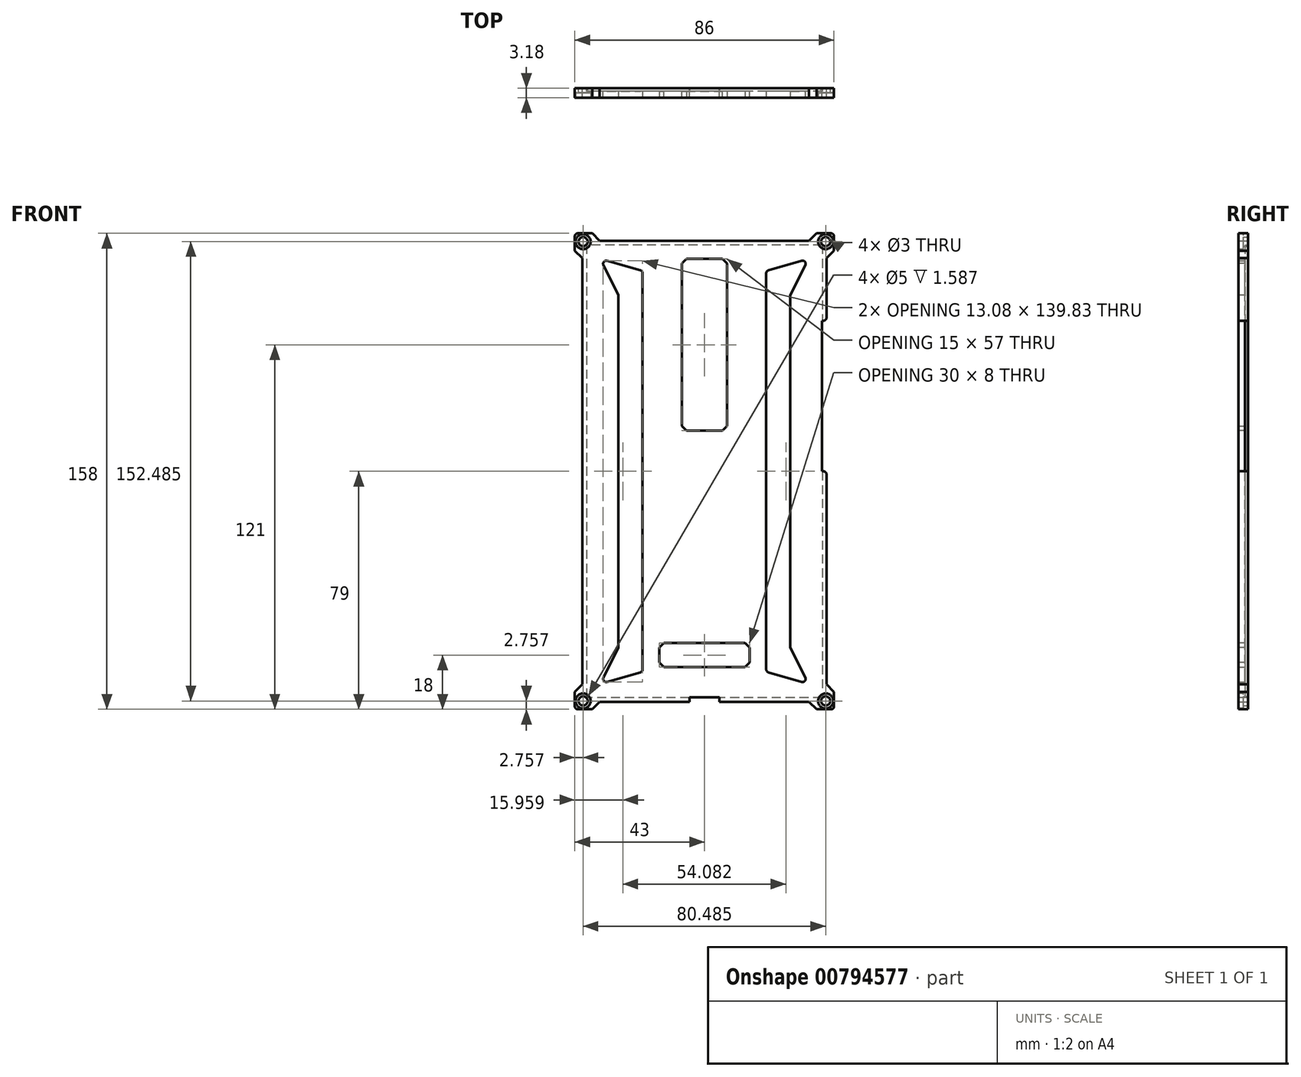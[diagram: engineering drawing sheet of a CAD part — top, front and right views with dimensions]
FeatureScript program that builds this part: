
annotation { "Feature Type Name" : "Feature", "Feature Type Description" : "" }
export const myFeature = defineFeature(function(context is Context, id is Id, definition is map)
    precondition{}
    {
        {
            var Q0;
            Q0=qCreatedBy(makeId("Front.planeOp"),FACE);
            var sketch = newSketch(context, id + "F0", { "sketchPlane" : qUnion([Q0])});
            skLineSegment(sketch, "E0.bottom", {"start": v(39, 75) * mm, "end": v(-39, 75) * mm});
            skLineSegment(sketch, "E0.top", {"start": v(39, -75) * mm, "end": v(-39, -75) * mm});
            skLineSegment(sketch, "E0.left", {"start": v(39, 75) * mm, "end": v(39, -75) * mm});
            skLineSegment(sketch, "E0.right", {"start": v(-39, 75) * mm, "end": v(-39, -75) * mm});
            skPoint(sketch, "E0.middle", {"position": v(0, 0) * mm});
            skSolve(sketch);
        }
        {
            var Q0;
            Q0=qCreatedBy(makeId("Front.planeOp"),FACE);
            var sketch = newSketch(context, id + "F1", { "sketchPlane" : qUnion([Q0])});
            skPoint(sketch, "E1.middle", {"position": v(0, 0) * mm});
            skLineSegment(sketch, "E2.bottom", {"start": v(43, 79) * mm, "end": v(37.24, 79) * mm});
            skLineSegment(sketch, "E2.top", {"start": v(43, -79) * mm, "end": v(37.24, -79) * mm});
            skLineSegment(sketch, "E2.left", {"start": v(43, 79) * mm, "end": v(43, 73.24) * mm});
            skLineSegment(sketch, "E2.right", {"start": v(-43, 79) * mm, "end": v(-43, 73.24) * mm});
            skLineSegment(sketch, "E3.bottom", {"start": v(40.5, 50) * mm, "end": v(39, 50) * mm});
            skLineSegment(sketch, "E3.top", {"start": v(40.5, 0) * mm, "end": v(39, 0) * mm});
            skLineSegment(sketch, "E3.right", {"start": v(39, 50) * mm, "end": v(39, 0) * mm});
            skLineSegment(sketch, "E4.trimOffspring", {"start": v(43, -73.24) * mm, "end": v(43, -79) * mm});
            skLineSegment(sketch, "E5.top", {"start": v(-5, -75) * mm, "end": v(5, -75) * mm});
            skLineSegment(sketch, "E5.left", {"start": v(-5, -76.5) * mm, "end": v(-5, -75) * mm});
            skLineSegment(sketch, "E5.right", {"start": v(5, -76.5) * mm, "end": v(5, -75) * mm});
            skLineSegment(sketch, "E6", {"start": v(0, 0) * mm, "end": v(0, -100.8) * mm, "construction": true});
            skLineSegment(sketch, "E7.trimOffspring", {"start": v(-37.24, -79) * mm, "end": v(-43, -79) * mm});
            skArc(sketch, "E8", {"start": v(7.5, 58.5) * mm, "mid": v(0, 66) * mm, "end": v(-7.5, 58.5) * mm});
            skArc(sketch, "E9", {"start": v(-7.5, 25.5) * mm, "mid": v(0, 18) * mm, "end": v(7.5, 25.5) * mm});
            skLineSegment(sketch, "E10", {"start": v(-7.5, 58.5) * mm, "end": v(-7.5, 25.5) * mm});
            skLineSegment(sketch, "E11", {"start": v(7.5, 58.5) * mm, "end": v(7.5, 25.5) * mm});
            skLineSegment(sketch, "E12.bottom", {"start": v(12, -59) * mm, "end": v(-12, -59) * mm});
            skLineSegment(sketch, "E12.top", {"start": v(12, -63) * mm, "end": v(-12, -63) * mm});
            skLineSegment(sketch, "E12.left", {"start": v(12, -59) * mm, "end": v(12, -63) * mm});
            skLineSegment(sketch, "E12.right", {"start": v(-12, -59) * mm, "end": v(-12, -63) * mm});
            skPoint(sketch, "E12.middle", {"position": v(0, -61) * mm});
            skLineSegment(sketch, "E13.bottom", {"start": v(36, 72) * mm, "end": v(-36, 72) * mm, "construction": true});
            skLineSegment(sketch, "E13.top", {"start": v(36, -72) * mm, "end": v(-36, -72) * mm, "construction": true});
            skLineSegment(sketch, "E13.left", {"start": v(36, 72) * mm, "end": v(36, -72) * mm, "construction": true});
            skLineSegment(sketch, "E13.right", {"start": v(-36, 72) * mm, "end": v(-36, -72) * mm, "construction": true});
            skLineSegment(sketch, "E14", {"start": v(36, 72) * mm, "end": v(43, 79) * mm, "construction": true});
            skLineSegment(sketch, "E15", {"start": v(-36, 72) * mm, "end": v(-43, 79) * mm, "construction": true});
            skLineSegment(sketch, "E16", {"start": v(36, -72) * mm, "end": v(43, -79) * mm, "construction": true});
            skLineSegment(sketch, "E17", {"start": v(-36, -72) * mm, "end": v(-43, -79) * mm, "construction": true});
            skCircle(sketch, "E18", {"center": v(-40.24, 76.24) * mm, "radius": 1.5 * mm});
            skCircle(sketch, "E19", {"center": v(40.24, 76.24) * mm, "radius": 1.5 * mm});
            skCircle(sketch, "E20", {"center": v(40.24, -76.24) * mm, "radius": 1.5 * mm});
            skCircle(sketch, "E21", {"center": v(-40.24, -76.24) * mm, "radius": 1.5 * mm});
            skLineSegment(sketch, "E22.top", {"start": v(-37.24, 76.5) * mm, "end": v(37.24, 76.5) * mm});
            skLineSegment(sketch, "E22.left", {"start": v(-37.24, 79) * mm, "end": v(-37.24, 76.5) * mm});
            skLineSegment(sketch, "E22.right", {"start": v(37.24, 79) * mm, "end": v(37.24, 76.5) * mm});
            skLineSegment(sketch, "E23.bottom", {"start": v(43, 73.24) * mm, "end": v(40.5, 73.24) * mm});
            skLineSegment(sketch, "E23.top", {"start": v(43, -73.24) * mm, "end": v(40.5, -73.24) * mm});
            skLineSegment(sketch, "E23.right", {"start": v(40.5, 73.24) * mm, "end": v(40.5, 50) * mm});
            skLineSegment(sketch, "E24.trimOffspring", {"start": v(40.5, 0) * mm, "end": v(40.5, -73.24) * mm});
            skLineSegment(sketch, "E25.top", {"start": v(37.24, -76.5) * mm, "end": v(5, -76.5) * mm});
            skLineSegment(sketch, "E25.left", {"start": v(37.24, -79) * mm, "end": v(37.24, -76.5) * mm});
            skLineSegment(sketch, "E25.right", {"start": v(-37.24, -79) * mm, "end": v(-37.24, -76.5) * mm});
            skLineSegment(sketch, "E26.trimOffspring", {"start": v(-5, -76.5) * mm, "end": v(-37.24, -76.5) * mm});
            skLineSegment(sketch, "E27.trimOffspring", {"start": v(-37.24, 79) * mm, "end": v(-43, 79) * mm});
            skLineSegment(sketch, "E28.bottom", {"start": v(-43, 73.24) * mm, "end": v(-40.5, 73.24) * mm});
            skLineSegment(sketch, "E28.top", {"start": v(-43, -73.24) * mm, "end": v(-40.5, -73.24) * mm});
            skLineSegment(sketch, "E28.right", {"start": v(-40.5, 73.24) * mm, "end": v(-40.5, -73.24) * mm});
            skLineSegment(sketch, "E29.trimOffspring", {"start": v(-43, -73.24) * mm, "end": v(-43, -79) * mm});
            skSolve(sketch);
        }
        {
            var Q0;
            Q0=qSketchRegion(id+"F1",true);
            extrude(context, id + "F2", {"entities" : qUnion([Q0]), "depth" : 3.17 * mm, "offsetDistance" : 25 * mm});
        }
        {
            var Q0;
            Q0=makeQuery(id+"F2.opExtrude","SWEPT_EDGE",EDGE,{"disambiguationData":[OSD([sQuery(id+"F1.wireOp",EDGE,"E22.top"),sQuery(id+"F1.wireOp",EDGE,"E22.left")])]});
            var Q1;
            Q1=makeQuery(id+"F2.opExtrude","SWEPT_EDGE",EDGE,{"disambiguationData":[OSD([sQuery(id+"F1.wireOp",EDGE,"E28.bottom"),sQuery(id+"F1.wireOp",EDGE,"E28.right")])]});
            var Q2;
            Q2=makeQuery(id+"F2.opExtrude","SWEPT_EDGE",EDGE,{"disambiguationData":[OSD([sQuery(id+"F1.wireOp",EDGE,"E22.top"),sQuery(id+"F1.wireOp",EDGE,"E22.right")])]});
            var Q3;
            Q3=makeQuery(id+"F2.opExtrude","SWEPT_EDGE",EDGE,{"disambiguationData":[OSD([sQuery(id+"F1.wireOp",EDGE,"E23.bottom"),sQuery(id+"F1.wireOp",EDGE,"E23.right")])]});
            var Q4;
            Q4=makeQuery(id+"F2.opExtrude","SWEPT_EDGE",EDGE,{"disambiguationData":[OSD([sQuery(id+"F1.wireOp",EDGE,"E23.top"),sQuery(id+"F1.wireOp",EDGE,"E24.trimOffspring")])]});
            var Q5;
            Q5=makeQuery(id+"F2.opExtrude","SWEPT_EDGE",EDGE,{"disambiguationData":[OSD([sQuery(id+"F1.wireOp",EDGE,"E25.top"),sQuery(id+"F1.wireOp",EDGE,"E25.left")])]});
            var Q6;
            Q6=makeQuery(id+"F2.opExtrude","SWEPT_EDGE",EDGE,{"disambiguationData":[OSD([sQuery(id+"F1.wireOp",EDGE,"E25.right"),sQuery(id+"F1.wireOp",EDGE,"E26.trimOffspring")])]});
            var Q7;
            Q7=makeQuery(id+"F2.opExtrude","SWEPT_EDGE",EDGE,{"disambiguationData":[OSD([sQuery(id+"F1.wireOp",EDGE,"E28.top"),sQuery(id+"F1.wireOp",EDGE,"E28.right")])]});
            chamfer(context, id + "F3", {"entities" : qUnion([Q0, Q1, Q2, Q3, Q4, Q5, Q6, Q7]), "width" : 2.5 * mm, "tangentPropagation" : true});
        }
        {
            var Q0;
            Q0=makeQuery(id+"F2.opExtrude","SWEPT_EDGE",EDGE,{"disambiguationData":[OSD([sQuery(id+"F1.wireOp",EDGE,"E2.bottom"),sQuery(id+"F1.wireOp",EDGE,"E2.left")])]});
            var Q1;
            Q1=makeQuery(id+"F2.opExtrude","SWEPT_EDGE",EDGE,{"disambiguationData":[OSD([sQuery(id+"F1.wireOp",EDGE,"E2.right"),sQuery(id+"F1.wireOp",EDGE,"E27.trimOffspring")])]});
            var Q2;
            Q2=makeQuery(id+"F2.opExtrude","SWEPT_EDGE",EDGE,{"disambiguationData":[OSD([sQuery(id+"F1.wireOp",EDGE,"E2.top"),sQuery(id+"F1.wireOp",EDGE,"E4.trimOffspring")])]});
            var Q3;
            Q3=makeQuery(id+"F2.opExtrude","SWEPT_EDGE",EDGE,{"disambiguationData":[OSD([sQuery(id+"F1.wireOp",EDGE,"E7.trimOffspring"),sQuery(id+"F1.wireOp",EDGE,"E29.trimOffspring")])]});
            var Q4;
            Q4=makeQuery(id+"F2.opExtrude","SWEPT_EDGE",EDGE,{"disambiguationData":[OSD([sQuery(id+"F1.wireOp",EDGE,"E3.bottom"),sQuery(id+"F1.wireOp",EDGE,"E23.right")])]});
            var Q5;
            Q5=makeQuery(id+"F2.opExtrude","SWEPT_EDGE",EDGE,{"disambiguationData":[OSD([sQuery(id+"F1.wireOp",EDGE,"E3.top"),sQuery(id+"F1.wireOp",EDGE,"E24.trimOffspring")])]});
            fillet(context, id + "F4", {"entities" : qUnion([Q0, Q1, Q2, Q3, Q4, Q5]), "radius" : 1 * mm, "tangentPropagation" : true, "allowEdgeOverflow" : false});
        }
        {
            var Q0;
            Q0=makeQuery(id+"F2.opExtrude","CAP_FACE",FACE,{"disambiguationData":[OSD([sQuery(id+"F1.wireOp",EDGE,"E2.bottom"),sQuery(id+"F1.wireOp",EDGE,"E2.top"),sQuery(id+"F1.wireOp",EDGE,"E2.left"),sQuery(id+"F1.wireOp",EDGE,"E2.right"),sQuery(id+"F1.wireOp",EDGE,"E3.bottom"),sQuery(id+"F1.wireOp",EDGE,"E3.top"),sQuery(id+"F1.wireOp",EDGE,"E3.right"),sQuery(id+"F1.wireOp",EDGE,"E4.trimOffspring"),sQuery(id+"F1.wireOp",EDGE,"E5.top"),sQuery(id+"F1.wireOp",EDGE,"E5.left"),sQuery(id+"F1.wireOp",EDGE,"E5.right"),sQuery(id+"F1.wireOp",EDGE,"E7.trimOffspring"),sQuery(id+"F1.wireOp",EDGE,"E8"),sQuery(id+"F1.wireOp",EDGE,"E9"),sQuery(id+"F1.wireOp",EDGE,"E10"),sQuery(id+"F1.wireOp",EDGE,"E11"),sQuery(id+"F1.wireOp",EDGE,"E12.bottom"),sQuery(id+"F1.wireOp",EDGE,"E12.top"),sQuery(id+"F1.wireOp",EDGE,"E12.left"),sQuery(id+"F1.wireOp",EDGE,"E12.right"),sQuery(id+"F1.wireOp",EDGE,"E18"),sQuery(id+"F1.wireOp",EDGE,"E19"),sQuery(id+"F1.wireOp",EDGE,"E20"),sQuery(id+"F1.wireOp",EDGE,"E21"),sQuery(id+"F1.wireOp",EDGE,"E22.top"),sQuery(id+"F1.wireOp",EDGE,"E22.left"),sQuery(id+"F1.wireOp",EDGE,"E22.right"),sQuery(id+"F1.wireOp",EDGE,"E23.bottom"),sQuery(id+"F1.wireOp",EDGE,"E23.top"),sQuery(id+"F1.wireOp",EDGE,"E23.right"),sQuery(id+"F1.wireOp",EDGE,"E24.trimOffspring"),sQuery(id+"F1.wireOp",EDGE,"E25.top"),sQuery(id+"F1.wireOp",EDGE,"E25.left"),sQuery(id+"F1.wireOp",EDGE,"E25.right"),sQuery(id+"F1.wireOp",EDGE,"E26.trimOffspring"),sQuery(id+"F1.wireOp",EDGE,"E27.trimOffspring"),sQuery(id+"F1.wireOp",EDGE,"E28.bottom"),sQuery(id+"F1.wireOp",EDGE,"E28.top"),sQuery(id+"F1.wireOp",EDGE,"E28.right"),sQuery(id+"F1.wireOp",EDGE,"E29.trimOffspring")])],"isStart":false});
            var sketch = newSketch(context, id + "F5", { "sketchPlane" : qUnion([Q0])});
            skCircle(sketch, "E30", {"center": v(-40.24, 76.24) * mm, "radius": 2.5 * mm});
            skCircle(sketch, "E31", {"center": v(40.24, 76.24) * mm, "radius": 2.5 * mm});
            skCircle(sketch, "E32", {"center": v(40.24, -76.24) * mm, "radius": 2.5 * mm});
            skCircle(sketch, "E33", {"center": v(-40.24, -76.24) * mm, "radius": 2.5 * mm});
            skSolve(sketch);
        }
        {
            var Q0;
            Q0 = qSketchRegion(id + "F5", true);
            extrude(context, id + "F6", {"entities" : qUnion([Q0]), "operationType" : NewBodyOperationType.REMOVE, "oppositeDirection" : true, "depth" : 1.59 * mm, "offsetDistance" : 25 * mm});
        }
        {
            var Q0;
            Q0=makeQuery(id+"F2.opExtrude","CAP_FACE",FACE,{"disambiguationData":[OSD([sQuery(id+"F1.wireOp",EDGE,"E2.bottom"),sQuery(id+"F1.wireOp",EDGE,"E2.top"),sQuery(id+"F1.wireOp",EDGE,"E2.left"),sQuery(id+"F1.wireOp",EDGE,"E2.right"),sQuery(id+"F1.wireOp",EDGE,"E3.bottom"),sQuery(id+"F1.wireOp",EDGE,"E3.top"),sQuery(id+"F1.wireOp",EDGE,"E3.right"),sQuery(id+"F1.wireOp",EDGE,"E4.trimOffspring"),sQuery(id+"F1.wireOp",EDGE,"E5.top"),sQuery(id+"F1.wireOp",EDGE,"E5.left"),sQuery(id+"F1.wireOp",EDGE,"E5.right"),sQuery(id+"F1.wireOp",EDGE,"E7.trimOffspring"),sQuery(id+"F1.wireOp",EDGE,"E8"),sQuery(id+"F1.wireOp",EDGE,"E9"),sQuery(id+"F1.wireOp",EDGE,"E10"),sQuery(id+"F1.wireOp",EDGE,"E11"),sQuery(id+"F1.wireOp",EDGE,"E12.bottom"),sQuery(id+"F1.wireOp",EDGE,"E12.top"),sQuery(id+"F1.wireOp",EDGE,"E12.left"),sQuery(id+"F1.wireOp",EDGE,"E12.right"),sQuery(id+"F1.wireOp",EDGE,"E18"),sQuery(id+"F1.wireOp",EDGE,"E19"),sQuery(id+"F1.wireOp",EDGE,"E20"),sQuery(id+"F1.wireOp",EDGE,"E21"),sQuery(id+"F1.wireOp",EDGE,"E22.top"),sQuery(id+"F1.wireOp",EDGE,"E22.left"),sQuery(id+"F1.wireOp",EDGE,"E22.right"),sQuery(id+"F1.wireOp",EDGE,"E23.bottom"),sQuery(id+"F1.wireOp",EDGE,"E23.top"),sQuery(id+"F1.wireOp",EDGE,"E23.right"),sQuery(id+"F1.wireOp",EDGE,"E24.trimOffspring"),sQuery(id+"F1.wireOp",EDGE,"E25.top"),sQuery(id+"F1.wireOp",EDGE,"E25.left"),sQuery(id+"F1.wireOp",EDGE,"E25.right"),sQuery(id+"F1.wireOp",EDGE,"E26.trimOffspring"),sQuery(id+"F1.wireOp",EDGE,"E27.trimOffspring"),sQuery(id+"F1.wireOp",EDGE,"E28.bottom"),sQuery(id+"F1.wireOp",EDGE,"E28.top"),sQuery(id+"F1.wireOp",EDGE,"E28.right"),sQuery(id+"F1.wireOp",EDGE,"E29.trimOffspring")])],"isStart":false});
            var sketch = newSketch(context, id + "F7", { "sketchPlane" : qUnion([Q0])});
            skLineSegment(sketch, "E34", {"start": v(-20.5, 66.5) * mm, "end": v(-20.5, -66.5) * mm});
            skLineSegment(sketch, "E35", {"start": v(-20.5, -66.5) * mm, "end": v(-34.5, -70.5) * mm});
            skLineSegment(sketch, "E36", {"start": v(-34.5, -70.5) * mm, "end": v(-28.5, -58.5) * mm});
            skLineSegment(sketch, "E37", {"start": v(-28.5, -58.5) * mm, "end": v(-28.5, 58.5) * mm});
            skLineSegment(sketch, "E38", {"start": v(-28.5, 58.5) * mm, "end": v(-34.5, 70.5) * mm});
            skLineSegment(sketch, "E39", {"start": v(-34.5, 70.5) * mm, "end": v(-20.5, 66.5) * mm});
            skLineSegment(sketch, "E40.MirrorCS", {"start": v(20.5, 66.5) * mm, "end": v(20.5, -66.5) * mm});
            skLineSegment(sketch, "E41.MirrorCS", {"start": v(34.5, 70.5) * mm, "end": v(20.5, 66.5) * mm});
            skLineSegment(sketch, "E42.MirrorCS", {"start": v(28.5, -58.5) * mm, "end": v(28.5, 58.5) * mm});
            skLineSegment(sketch, "E43.MirrorCS", {"start": v(28.5, 58.5) * mm, "end": v(34.5, 70.5) * mm});
            skLineSegment(sketch, "E44.MirrorCS", {"start": v(20.5, -66.5) * mm, "end": v(34.5, -70.5) * mm});
            skLineSegment(sketch, "E45.MirrorCS", {"start": v(34.5, -70.5) * mm, "end": v(28.5, -58.5) * mm});
            skLineSegment(sketch, "E46", {"start": v(0, 70.5) * mm, "end": v(0, 13.5) * mm, "construction": true});
            skLineSegment(sketch, "E47", {"start": v(-7.5, 58.5) * mm, "end": v(-7.5, 71.8) * mm, "construction": true});
            skLineSegment(sketch, "E48", {"start": v(0, 70.5) * mm, "end": v(-7.5, 70.5) * mm, "construction": true});
            skLineSegment(sketch, "E49", {"start": v(0, 13.5) * mm, "end": v(10.16, 13.5) * mm, "construction": true});
            skLineSegment(sketch, "E50", {"start": v(7.5, 25.5) * mm, "end": v(7.5, 13.5) * mm, "construction": true});
            skLineSegment(sketch, "E51.bottom", {"start": v(-7.5, 70.5) * mm, "end": v(7.5, 70.5) * mm});
            skLineSegment(sketch, "E51.top", {"start": v(-7.5, 13.5) * mm, "end": v(7.5, 13.5) * mm});
            skLineSegment(sketch, "E51.left", {"start": v(-7.5, 70.5) * mm, "end": v(-7.5, 13.5) * mm});
            skLineSegment(sketch, "E51.right", {"start": v(7.5, 70.5) * mm, "end": v(7.5, 13.5) * mm});
            skLineSegment(sketch, "E52", {"start": v(-12, -63) * mm, "end": v(12, -59) * mm, "construction": true});
            skLineSegment(sketch, "E53", {"start": v(-12, -59) * mm, "end": v(12, -63) * mm, "construction": true});
            skLineSegment(sketch, "E54.bottom", {"start": v(15, -57) * mm, "end": v(-15, -57) * mm});
            skLineSegment(sketch, "E54.top", {"start": v(15, -65) * mm, "end": v(-15, -65) * mm});
            skLineSegment(sketch, "E54.left", {"start": v(15, -57) * mm, "end": v(15, -65) * mm});
            skLineSegment(sketch, "E54.right", {"start": v(-15, -57) * mm, "end": v(-15, -65) * mm});
            skPoint(sketch, "E54.middle", {"position": v(0, -61) * mm});
            skSolve(sketch);
        }
        {
            var Q0;
            Q0 = qSketchRegion(id + "F7", true);
            extrude(context, id + "F8", {"entities" : qUnion([Q0]), "operationType" : NewBodyOperationType.REMOVE, "endBound" : BoundingType.THROUGH_ALL, "oppositeDirection" : true, "depth" : 25 * mm, "offsetDistance" : 25 * mm});
        }
        {
            var Q0;
            Q0=makeQuery(id+"F8.boolean.opBoolean","COPY",EDGE,{"derivedFrom":makeQuery(id+"F8.opExtrude","SWEPT_EDGE",EDGE,{"disambiguationData":[OSD([sQuery(id+"F7.wireOp",EDGE,"E51.bottom"),sQuery(id+"F7.wireOp",EDGE,"E51.right")])]})});
            var Q1;
            Q1=makeQuery(id+"F8.boolean.opBoolean","COPY",EDGE,{"derivedFrom":makeQuery(id+"F8.opExtrude","SWEPT_EDGE",EDGE,{"disambiguationData":[OSD([sQuery(id+"F7.wireOp",EDGE,"E51.bottom"),sQuery(id+"F7.wireOp",EDGE,"E51.left")])]})});
            var Q2;
            Q2=makeQuery(id+"F8.boolean.opBoolean","COPY",EDGE,{"derivedFrom":makeQuery(id+"F8.opExtrude","SWEPT_EDGE",EDGE,{"disambiguationData":[OSD([sQuery(id+"F7.wireOp",EDGE,"E51.top"),sQuery(id+"F7.wireOp",EDGE,"E51.left")])]})});
            var Q3;
            Q3=makeQuery(id+"F8.boolean.opBoolean","COPY",EDGE,{"derivedFrom":makeQuery(id+"F8.opExtrude","SWEPT_EDGE",EDGE,{"disambiguationData":[OSD([sQuery(id+"F7.wireOp",EDGE,"E51.top"),sQuery(id+"F7.wireOp",EDGE,"E51.right")])]})});
            chamfer(context, id + "F9", {"entities" : qUnion([Q0, Q1, Q2, Q3]), "width" : 1.5 * mm, "tangentPropagation" : true});
        }
        {
            var Q0;
            Q0=makeQuery(id+"F8.boolean.opBoolean","COPY",EDGE,{"derivedFrom":makeQuery(id+"F8.opExtrude","SWEPT_EDGE",EDGE,{"disambiguationData":[OSD([sQuery(id+"F7.wireOp",EDGE,"E54.top"),sQuery(id+"F7.wireOp",EDGE,"E54.right")])]})});
            var Q1;
            Q1=makeQuery(id+"F8.boolean.opBoolean","COPY",EDGE,{"derivedFrom":makeQuery(id+"F8.opExtrude","SWEPT_EDGE",EDGE,{"disambiguationData":[OSD([sQuery(id+"F7.wireOp",EDGE,"E54.bottom"),sQuery(id+"F7.wireOp",EDGE,"E54.right")])]})});
            var Q2;
            Q2=makeQuery(id+"F8.boolean.opBoolean","COPY",EDGE,{"derivedFrom":makeQuery(id+"F8.opExtrude","SWEPT_EDGE",EDGE,{"disambiguationData":[OSD([sQuery(id+"F7.wireOp",EDGE,"E54.bottom"),sQuery(id+"F7.wireOp",EDGE,"E54.left")])]})});
            var Q3;
            Q3=makeQuery(id+"F8.boolean.opBoolean","COPY",EDGE,{"derivedFrom":makeQuery(id+"F8.opExtrude","SWEPT_EDGE",EDGE,{"disambiguationData":[OSD([sQuery(id+"F7.wireOp",EDGE,"E54.top"),sQuery(id+"F7.wireOp",EDGE,"E54.left")])]})});
            chamfer(context, id + "F10", {"entities" : qUnion([Q0, Q1, Q2, Q3]), "width" : 1.5 * mm, "tangentPropagation" : true});
        }
        {
            var Q0;
            Q0=makeQuery(id+"F8.boolean.opBoolean","COPY",EDGE,{"derivedFrom":makeQuery(id+"F8.opExtrude","SWEPT_EDGE",EDGE,{"disambiguationData":[OSD([sQuery(id+"F7.wireOp",EDGE,"E38"),sQuery(id+"F7.wireOp",EDGE,"E39")])]})});
            var Q1;
            Q1=makeQuery(id+"F8.boolean.opBoolean","COPY",EDGE,{"derivedFrom":makeQuery(id+"F8.opExtrude","SWEPT_EDGE",EDGE,{"disambiguationData":[OSD([sQuery(id+"F7.wireOp",EDGE,"E34"),sQuery(id+"F7.wireOp",EDGE,"E39")])]})});
            var Q2;
            Q2=makeQuery(id+"F8.boolean.opBoolean","COPY",EDGE,{"derivedFrom":makeQuery(id+"F8.opExtrude","SWEPT_EDGE",EDGE,{"disambiguationData":[OSD([sQuery(id+"F7.wireOp",EDGE,"E40.MirrorCS"),sQuery(id+"F7.wireOp",EDGE,"E41.MirrorCS")])]})});
            var Q3;
            Q3=makeQuery(id+"F8.boolean.opBoolean","COPY",EDGE,{"derivedFrom":makeQuery(id+"F8.opExtrude","SWEPT_EDGE",EDGE,{"disambiguationData":[OSD([sQuery(id+"F7.wireOp",EDGE,"E41.MirrorCS"),sQuery(id+"F7.wireOp",EDGE,"E43.MirrorCS")])]})});
            var Q4;
            Q4=makeQuery(id+"F8.boolean.opBoolean","COPY",EDGE,{"derivedFrom":makeQuery(id+"F8.opExtrude","SWEPT_EDGE",EDGE,{"disambiguationData":[OSD([sQuery(id+"F7.wireOp",EDGE,"E44.MirrorCS"),sQuery(id+"F7.wireOp",EDGE,"E45.MirrorCS")])]})});
            var Q5;
            Q5=makeQuery(id+"F8.boolean.opBoolean","COPY",EDGE,{"derivedFrom":makeQuery(id+"F8.opExtrude","SWEPT_EDGE",EDGE,{"disambiguationData":[OSD([sQuery(id+"F7.wireOp",EDGE,"E40.MirrorCS"),sQuery(id+"F7.wireOp",EDGE,"E44.MirrorCS")])]})});
            var Q6;
            Q6=makeQuery(id+"F8.boolean.opBoolean","COPY",EDGE,{"derivedFrom":makeQuery(id+"F8.opExtrude","SWEPT_EDGE",EDGE,{"disambiguationData":[OSD([sQuery(id+"F7.wireOp",EDGE,"E35"),sQuery(id+"F7.wireOp",EDGE,"E36")])]})});
            var Q7;
            Q7=makeQuery(id+"F8.boolean.opBoolean","COPY",EDGE,{"derivedFrom":makeQuery(id+"F8.opExtrude","SWEPT_EDGE",EDGE,{"disambiguationData":[OSD([sQuery(id+"F7.wireOp",EDGE,"E34"),sQuery(id+"F7.wireOp",EDGE,"E35")])]})});
            fillet(context, id + "F11", {"entities" : qUnion([Q0, Q1, Q2, Q3, Q4, Q5, Q6, Q7]), "radius" : 1 * mm, "tangentPropagation" : true, "allowEdgeOverflow" : false});
        }
        {
            var Q0;
            Q0=makeQuery(id+"F2.opExtrude","CAP_FACE",FACE,{"disambiguationData":[OSD([sQuery(id+"F1.wireOp",EDGE,"E2.bottom"),sQuery(id+"F1.wireOp",EDGE,"E2.top"),sQuery(id+"F1.wireOp",EDGE,"E2.left"),sQuery(id+"F1.wireOp",EDGE,"E2.right"),sQuery(id+"F1.wireOp",EDGE,"E3.bottom"),sQuery(id+"F1.wireOp",EDGE,"E3.top"),sQuery(id+"F1.wireOp",EDGE,"E3.right"),sQuery(id+"F1.wireOp",EDGE,"E4.trimOffspring"),sQuery(id+"F1.wireOp",EDGE,"E5.top"),sQuery(id+"F1.wireOp",EDGE,"E5.left"),sQuery(id+"F1.wireOp",EDGE,"E5.right"),sQuery(id+"F1.wireOp",EDGE,"E7.trimOffspring"),sQuery(id+"F1.wireOp",EDGE,"E8"),sQuery(id+"F1.wireOp",EDGE,"E9"),sQuery(id+"F1.wireOp",EDGE,"E10"),sQuery(id+"F1.wireOp",EDGE,"E11"),sQuery(id+"F1.wireOp",EDGE,"E12.bottom"),sQuery(id+"F1.wireOp",EDGE,"E12.top"),sQuery(id+"F1.wireOp",EDGE,"E12.left"),sQuery(id+"F1.wireOp",EDGE,"E12.right"),sQuery(id+"F1.wireOp",EDGE,"E18"),sQuery(id+"F1.wireOp",EDGE,"E19"),sQuery(id+"F1.wireOp",EDGE,"E20"),sQuery(id+"F1.wireOp",EDGE,"E21"),sQuery(id+"F1.wireOp",EDGE,"E22.top"),sQuery(id+"F1.wireOp",EDGE,"E22.left"),sQuery(id+"F1.wireOp",EDGE,"E22.right"),sQuery(id+"F1.wireOp",EDGE,"E23.bottom"),sQuery(id+"F1.wireOp",EDGE,"E23.top"),sQuery(id+"F1.wireOp",EDGE,"E23.right"),sQuery(id+"F1.wireOp",EDGE,"E24.trimOffspring"),sQuery(id+"F1.wireOp",EDGE,"E25.top"),sQuery(id+"F1.wireOp",EDGE,"E25.left"),sQuery(id+"F1.wireOp",EDGE,"E25.right"),sQuery(id+"F1.wireOp",EDGE,"E26.trimOffspring"),sQuery(id+"F1.wireOp",EDGE,"E27.trimOffspring"),sQuery(id+"F1.wireOp",EDGE,"E28.bottom"),sQuery(id+"F1.wireOp",EDGE,"E28.top"),sQuery(id+"F1.wireOp",EDGE,"E28.right"),sQuery(id+"F1.wireOp",EDGE,"E29.trimOffspring")])],"isStart":true});
            var sketch = newSketch(context, id + "F12", { "sketchPlane" : qUnion([Q0])});
            skLineSegment(sketch, "E55.bottom", {"start": v(-39.12, 75.12) * mm, "end": v(39.13, 75.12) * mm});
            skLineSegment(sketch, "E55.top", {"start": v(-39.13, -75.12) * mm, "end": v(39.12, -75.12) * mm});
            skLineSegment(sketch, "E55.left", {"start": v(-39.12, 75.12) * mm, "end": v(-39.13, -75.12) * mm});
            skLineSegment(sketch, "E55.right", {"start": v(39.13, 75.12) * mm, "end": v(39.12, -75.12) * mm});
            skPoint(sketch, "E55.middle", {"position": v(0, 0) * mm});
            skSolve(sketch);
        }
        {
            var Q0;
            Q0 = qSketchRegion(id + "F12", true);
            extrude(context, id + "F13", {"entities" : qUnion([Q0]), "operationType" : NewBodyOperationType.REMOVE, "oppositeDirection" : true, "depth" : 1 * mm, "offsetDistance" : 25 * mm});
        }
    });
